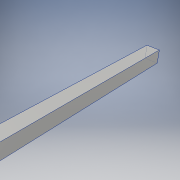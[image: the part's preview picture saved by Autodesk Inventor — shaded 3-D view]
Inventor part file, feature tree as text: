
AUTODESK INVENTOR PART (.ipt)
format: ipt  version: 2019 (Build 230136000, 136)  size: 93,696 bytes
history: native  units: in
note: dims shown in document units (in); Inventor stores cm internally (conversion verified against a paired STEP export)
features: extrude x1, sketch x1
ambient origin geometry x8: Origin, YZ Plane, XZ Plane, XY Plane, X Axis, Y Axis, Z Axis, Center Point
bodies: Solid1 (feature_tree)
feature tree (2):
  extrude  "Extrusion1"  Depth=12.0in TaperAngle=0.0deg
  sketch  "Sketch1"  dims[d0=1.0in d1=12.0in d2=0.0in]
